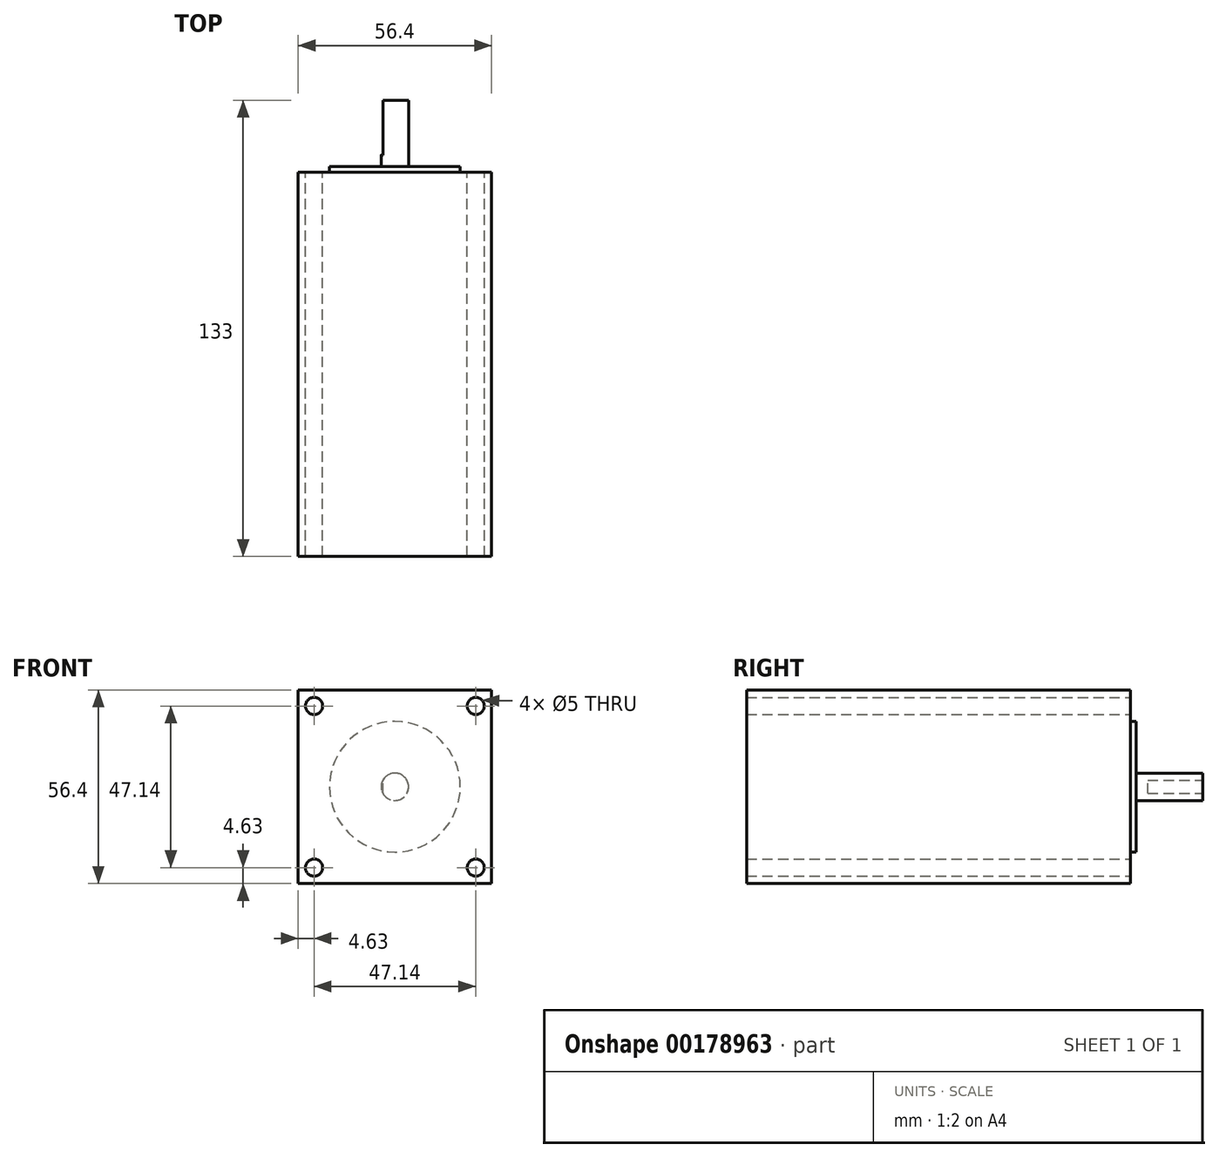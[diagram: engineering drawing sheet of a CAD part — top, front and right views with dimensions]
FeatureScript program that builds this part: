
annotation { "Feature Type Name" : "Feature", "Feature Type Description" : "" }
export const myFeature = defineFeature(function(context is Context, id is Id, definition is map)
    precondition{}
    {
        {
            var Q0;
            Q0=qCreatedBy(makeId("Front.planeOp"),FACE);
            var sketch = newSketch(context, id + "F0", { "sketchPlane" : qUnion([Q0])});
            skLineSegment(sketch, "E0.bottom", {"start": v(28.2, -28.2) * mm, "end": v(-28.2, -28.2) * mm});
            skLineSegment(sketch, "E0.top", {"start": v(28.2, 28.2) * mm, "end": v(-28.2, 28.2) * mm});
            skLineSegment(sketch, "E0.left", {"start": v(28.2, -28.2) * mm, "end": v(28.2, 28.2) * mm});
            skLineSegment(sketch, "E0.right", {"start": v(-28.2, -28.2) * mm, "end": v(-28.2, 28.2) * mm});
            skPoint(sketch, "E0.middle", {"position": v(0, 0) * mm});
            skCircle(sketch, "E1", {"center": v(0, 0) * mm, "radius": 19.05 * mm});
            skCircle(sketch, "E2", {"center": v(0, 0) * mm, "radius": 4 * mm});
            skCircle(sketch, "E3", {"center": v(-23.57, 23.57) * mm, "radius": 2.5 * mm});
            skCircle(sketch, "E4", {"center": v(23.57, 23.57) * mm, "radius": 2.5 * mm});
            skCircle(sketch, "E5", {"center": v(-23.57, -23.57) * mm, "radius": 2.5 * mm});
            skCircle(sketch, "E6", {"center": v(23.57, -23.57) * mm, "radius": 2.5 * mm});
            skPoint(sketch, "E7.orphan", {"position": v(-23.57, 28.2) * mm});
            skPoint(sketch, "E8.start.orphan", {"position": v(-28.2, 23.57) * mm});
            skPoint(sketch, "E9.start.orphan", {"position": v(23.57, 28.2) * mm});
            skPoint(sketch, "E10.trimOffspring.end.orphan", {"position": v(23.57, -28.2) * mm});
            skPoint(sketch, "E11.start.orphan", {"position": v(-28.2, -23.57) * mm});
            skPoint(sketch, "E12.end.orphan", {"position": v(-23.57, -28.2) * mm});
            skSolve(sketch);
        }
        {
            var Q0;
            Q0=makeQuery(id+"F0.imprint","IMPRINT",FACE,{"disambiguationData":[TD([[makeQuery(id+"F0.imprint","IMPRINT",EDGE,{"derivedFrom":sQuery(id+"F0.wireOp",EDGE,"E1")}),1.0]])]});
            var Q1;
            Q1=makeQuery(id+"F0.imprint","IMPRINT",FACE,{"disambiguationData":[TD([[makeQuery(id+"F0.imprint","IMPRINT",EDGE,{"derivedFrom":sQuery(id+"F0.wireOp",EDGE,"E2")}),1.0]])]});
            var Q2;
            Q2=makeQuery(id+"F0.imprint","IMPRINT",FACE,{"disambiguationData":[TD([[makeQuery(id+"F0.imprint","IMPRINT",EDGE,{"derivedFrom":sQuery(id+"F0.wireOp",EDGE,"E0.bottom")}),-1.0]])]});
            extrude(context, id + "F1", {"entities" : qUnion([Q0, Q1, Q2]), "depth" : 112 * mm});
        }
        {
            var Q0;
            Q0=makeQuery(id+"F0.imprint","IMPRINT",FACE,{"disambiguationData":[TD([[makeQuery(id+"F0.imprint","IMPRINT",EDGE,{"derivedFrom":sQuery(id+"F0.wireOp",EDGE,"E1")}),1.0]])]});
            extrude(context, id + "F2", {"entities" : qUnion([Q0]), "operationType" : NewBodyOperationType.ADD, "oppositeDirection" : true, "depth" : 1.6 * mm});
        }
        {
            var Q0;
            Q0=makeQuery(id+"F0.imprint","IMPRINT",FACE,{"disambiguationData":[TD([[makeQuery(id+"F0.imprint","IMPRINT",EDGE,{"derivedFrom":sQuery(id+"F0.wireOp",EDGE,"E2")}),1.0]])]});
            extrude(context, id + "F3", {"entities" : qUnion([Q0]), "operationType" : NewBodyOperationType.ADD, "oppositeDirection" : true, "depth" : 21 * mm});
        }
        {
            var Q0;
            Q0=makeQuery(id+"F3.opExtrude","CAP_FACE",FACE,{"disambiguationData":[OSD([sQuery(id+"F0.wireOp",EDGE,"E2")])],"isStart":false});
            var sketch = newSketch(context, id + "F4", { "sketchPlane" : qUnion([Q0])});
            skLineSegment(sketch, "E13", {"start": v(-4, 0) * mm, "end": v(3.5, 0) * mm});
            skLineSegment(sketch, "E14", {"start": v(3.5, 0) * mm, "end": v(3.5, -1.92) * mm});
            skLineSegment(sketch, "E15", {"start": v(3.5, -1.92) * mm, "end": v(3.5, 1.92) * mm});
            skArc(sketch, "E16", {"start": v(3.5, -1.92) * mm, "mid": v(4, 0) * mm, "end": v(3.5, 1.92) * mm});
            skSolve(sketch);
        }
        {
            var Q0;
            {var subQ2=sQuery(id+"F4.wireOp",EDGE,"E16");Q0=makeQuery(id+"F4.imprint","IMPRINT",FACE,{"disambiguationData":[TD([[makeQuery(id+"F4.imprint","IMPRINT",EDGE,{"derivedFrom":subQ2}),1.0]])]});}
            extrude(context, id + "F5", {"entities" : qUnion([Q0]), "operationType" : NewBodyOperationType.REMOVE, "oppositeDirection" : true, "depth" : 16 * mm});
        }
    });
